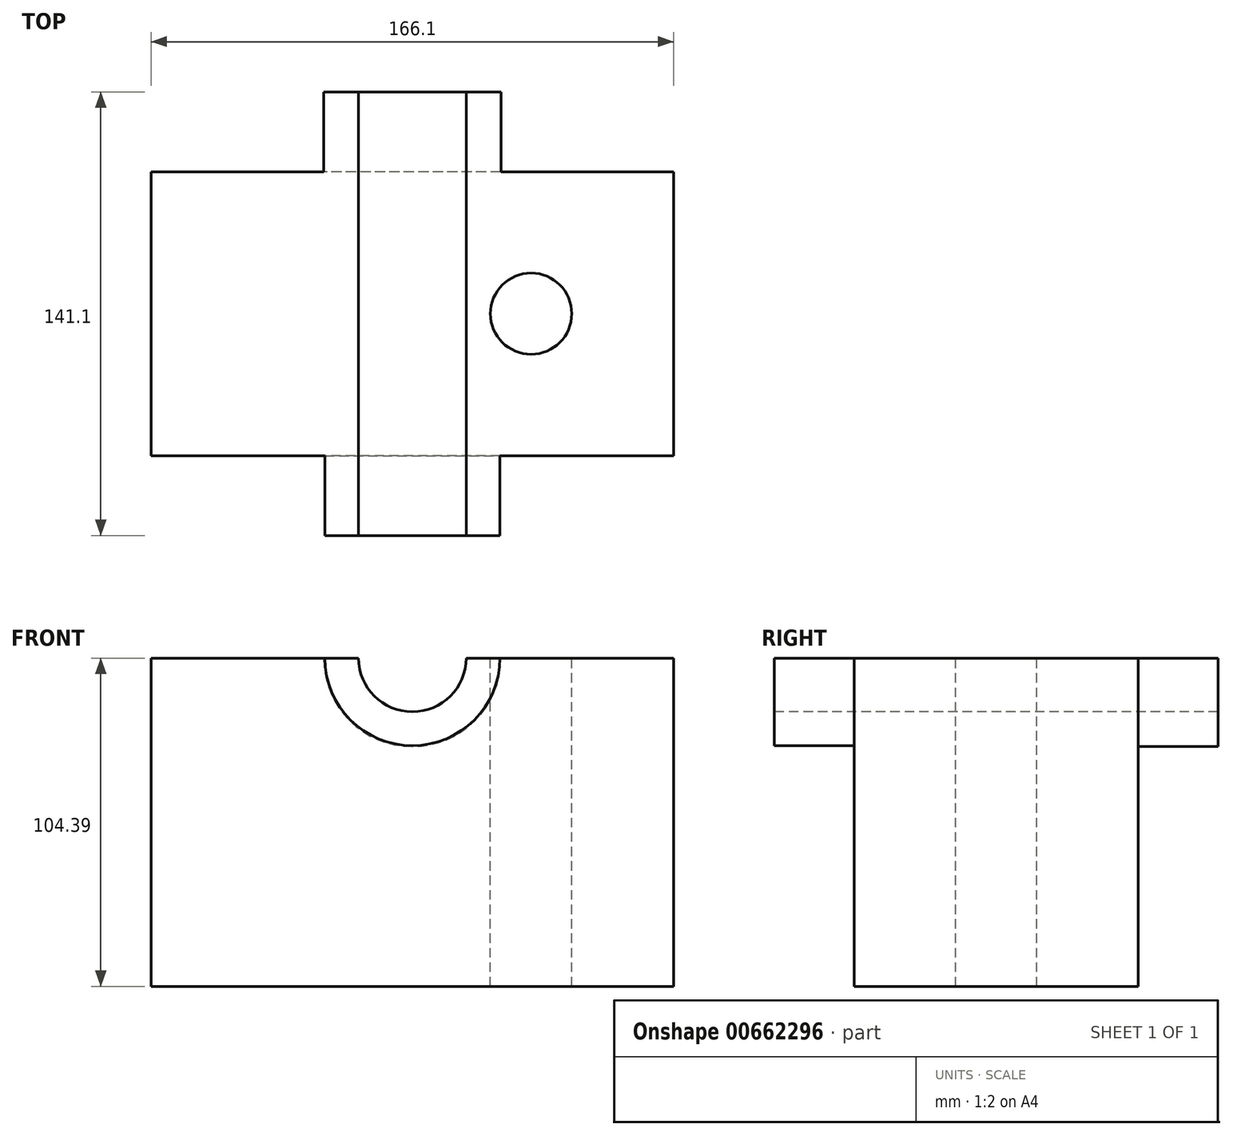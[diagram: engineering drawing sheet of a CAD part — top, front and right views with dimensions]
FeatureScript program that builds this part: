
annotation { "Feature Type Name" : "Feature", "Feature Type Description" : "" }
export const myFeature = defineFeature(function(context is Context, id is Id, definition is map)
    precondition{}
    {
        {
            var Q0;
            Q0=qCreatedBy(makeId("Top.planeOp"),FACE);
            var sketch = newSketch(context, id + "F0", { "sketchPlane" : qUnion([Q0])});
            skLineSegment(sketch, "E0.bottom", {"start": v(83.05, 45.15) * mm, "end": v(-83.05, 45.15) * mm});
            skLineSegment(sketch, "E0.top", {"start": v(83.05, -45.15) * mm, "end": v(-83.05, -45.15) * mm});
            skLineSegment(sketch, "E0.left", {"start": v(83.05, 45.15) * mm, "end": v(83.05, -45.15) * mm});
            skLineSegment(sketch, "E0.right", {"start": v(-83.05, 45.15) * mm, "end": v(-83.05, -45.15) * mm});
            skPoint(sketch, "E0.middle", {"position": v(0, 0) * mm});
            skSolve(sketch);
        }
        {
            var Q0;
            Q0 = qSketchRegion(id + "F0", true);
            extrude(context, id + "F1", {"entities" : qUnion([Q0]), "depth" : 104.4 * mm, "offsetDistance" : 25.4 * mm});
        }
        {
            var Q0;
            Q0=makeQuery(id+"F1.opExtrude","SWEPT_FACE",FACE,{"disambiguationData":[OSD([sQuery(id+"F0.wireOp",EDGE,"E0.bottom")])]});
            var sketch = newSketch(context, id + "F2", { "sketchPlane" : qUnion([Q0])});
            skCircle(sketch, "E1", {"center": v(0, 104.4) * mm, "radius": 17.08 * mm});
            skCircle(sketch, "E2", {"center": v(0, 104.4) * mm, "radius": 28.15 * mm});
            skSolve(sketch);
        }
        {
            var Q0;
            {var subQ0=sQuery(id+"F2.wireOp",EDGE,"E1");var subQ1=makeQuery(id+"F1.opExtrude","CAP_EDGE",EDGE,{"disambiguationData":[OSD([sQuery(id+"F0.wireOp",EDGE,"E0.bottom")])],"isStart":false});var subQ2=makeQuery(id+"F2.imprint","INTERSECT",VERTEX,{"disambiguationData":[OD(0.0)],"derivedFrom":[subQ1,subQ0]});Q0=makeQuery(id+"F2.imprint","IMPRINT",FACE,{"disambiguationData":[TD([[makeQuery(id+"F2.imprint","IMPRINT",EDGE,{"disambiguationData":[TD([[subQ2,-1.0]])],"derivedFrom":subQ0}),-1.0]])]});}
            var Q1;
            Q1=makeQuery(id+"F1.opExtrude","SWEPT_FACE",FACE,{"disambiguationData":[OSD([sQuery(id+"F0.wireOp",EDGE,"E0.top")])]});
            extrude(context, id + "F3", {"entities" : qUnion([Q0, Q1]), "operationType" : NewBodyOperationType.ADD, "depth" : 25.4 * mm, "offsetDistance" : 25.4 * mm});
        }
        {
            var Q0;
            {var subQ0=sQuery(id+"F0.wireOp",EDGE,"E0.bottom");var subQ3=sQuery(id+"F2.wireOp",EDGE,"E1");Q0=makeQuery(id+"F3.boolean.opBoolean","SPLIT",FACE,{"disambiguationData":[TD([makeQuery(id+"F3.opExtrude","SWEPT_FACE",FACE,{"disambiguationData":[OSD([subQ3])]})])],"derivedFrom":makeQuery(id+"F1.opExtrude","SWEPT_FACE",FACE,{"disambiguationData":[OSD([subQ0])]})});}
            var sketch = newSketch(context, id + "F4", { "sketchPlane" : qUnion([Q0])});
            skSolve(sketch);
        }
        {
            var Q0;
            {var subQ0=sQuery(id+"F2.wireOp",EDGE,"E1");Q0=makeQuery(id+"F4.imprint","IMPRINT",FACE,{"disambiguationData":[TD([[makeQuery(id+"F4.imprint","IMPRINT",EDGE,{"derivedFrom":makeQuery(id+"F3.opExtrude","CAP_EDGE",EDGE,{"disambiguationData":[OSD([subQ0])],"isStart":true})}),1.0]])]});}
            extrude(context, id + "F5", {"entities" : qUnion([Q0]), "operationType" : NewBodyOperationType.REMOVE, "oppositeDirection" : true, "depth" : 306.32 * mm, "offsetDistance" : 25.4 * mm});
        }
        {
            var Q0;
            Q0=makeQuery(id+"F1.opExtrude","SWEPT_FACE",FACE,{"disambiguationData":[OSD([sQuery(id+"F0.wireOp",EDGE,"E0.top")])]});
            var sketch = newSketch(context, id + "F6", { "sketchPlane" : qUnion([Q0])});
            skCircle(sketch, "E3", {"center": v(0, 104.4) * mm, "radius": 16.53 * mm});
            skCircle(sketch, "E4", {"center": v(0, 104.4) * mm, "radius": 27.83 * mm});
            skSolve(sketch);
        }
        {
            var Q0;
            {var subQ1=sQuery(id+"F2.wireOp",EDGE,"E1");var subQ4=sQuery(id+"F0.wireOp",EDGE,"E0.top");var subQ5=makeQuery(id+"F1.opExtrude","SWEPT_FACE",FACE,{"disambiguationData":[OSD([subQ4])]});var subQ13=makeQuery(id+"F5.opExtrude","SWEPT_FACE",FACE,{"disambiguationData":[OSD([subQ1])]});var subQ19=makeQuery(id+"F5.boolean.opBoolean","INTERSECT",EDGE,{"derivedFrom":[subQ5,subQ13]});Q0=makeQuery(id+"F6.imprint","IMPRINT",FACE,{"disambiguationData":[TD([[makeQuery(id+"F6.imprint","IMPRINT",EDGE,{"derivedFrom":subQ19}),-1.0]])]});}
            extrude(context, id + "F7", {"entities" : qUnion([Q0]), "operationType" : NewBodyOperationType.ADD, "depth" : 25.4 * mm, "offsetDistance" : 25.4 * mm});
        }
        {
            var Q0;
            {var subQ2=sQuery(id+"F0.wireOp",EDGE,"E0.left");var subQ3=makeQuery(id+"F1.opExtrude","SWEPT_FACE",FACE,{"disambiguationData":[OSD([subQ2])]});var subQ4=sQuery(id+"F0.wireOp",EDGE,"E0.top");var subQ6=sQuery(id+"F0.wireOp",EDGE,"E0.bottom");var subQ7=makeQuery(id+"F1.opExtrude","CAP_FACE",FACE,{"disambiguationData":[OSD([subQ6,subQ4,subQ2,sQuery(id+"F0.wireOp",EDGE,"E0.right")])],"isStart":false});var subQ8=sQuery(id+"F2.wireOp",EDGE,"E2");var subQ9=makeQuery(id+"F1.opExtrude","CAP_EDGE",EDGE,{"disambiguationData":[OSD([subQ6])],"isStart":false});var subQ10=makeQuery(id+"F3.opExtrude","SWEPT_FACE",FACE,{"disambiguationData":[OSD([subQ6]),TDD([makeQuery(id+"F2.imprint","IMPRINT",EDGE,{"disambiguationData":[TD([[makeQuery(id+"F2.imprint","INTERSECT",VERTEX,{"disambiguationData":[OD(0.0)],"derivedFrom":[subQ9,subQ8]}),-1.0]])],"derivedFrom":subQ9})])]});var subQ11=makeQuery(id+"F3.opExtrude","SWEPT_FACE",FACE,{"disambiguationData":[OSD([subQ6]),TDD([makeQuery(id+"F2.imprint","IMPRINT",EDGE,{"disambiguationData":[TD([[makeQuery(id+"F2.imprint","INTERSECT",VERTEX,{"disambiguationData":[OD(1.0)],"derivedFrom":[subQ9,subQ8]}),1.0]])],"derivedFrom":subQ9})])]});var subQ13=makeQuery(id+"F5.boolean.opBoolean","SPLIT",EDGE,{"disambiguationData":[TD([subQ3])],"derivedFrom":makeQuery(id+"F1.opExtrude","CAP_EDGE",EDGE,{"disambiguationData":[OSD([subQ4])],"isStart":false})});Q0=makeQuery(id+"F7.boolean.opBoolean","MERGE",FACE,{"derivedFrom":[makeQuery(id+"F5.boolean.opBoolean","SPLIT",FACE,{"disambiguationData":[TD([subQ3])],"derivedFrom":makeQuery(id+"F3.boolean.opBoolean","MERGE",FACE,{"derivedFrom":[subQ7,subQ10,subQ11]})}),makeQuery(id+"F7.opExtrude","SWEPT_FACE",FACE,{"disambiguationData":[OSD([subQ4]),TDD([makeQuery(id+"F6.imprint","IMPRINT",EDGE,{"disambiguationData":[TD([[makeQuery(id+"F6.imprint","INTERSECT",VERTEX,{"derivedFrom":[subQ13,sQuery(id+"F6.wireOp",EDGE,"E4")]}),-1.0]])],"derivedFrom":subQ13})])]})]});}
            var sketch = newSketch(context, id + "F8", { "sketchPlane" : qUnion([Q0])});
            skCircle(sketch, "E5", {"center": v(37.74, 0) * mm, "radius": 12.92 * mm});
            skSolve(sketch);
        }
        {
            var Q0;
            Q0 = qSketchRegion(id + "F8", true);
            extrude(context, id + "F9", {"entities" : qUnion([Q0]), "operationType" : NewBodyOperationType.REMOVE, "endBound" : BoundingType.THROUGH_ALL, "oppositeDirection" : true, "depth" : 25.4 * mm, "offsetDistance" : 25.4 * mm});
        }
    });
